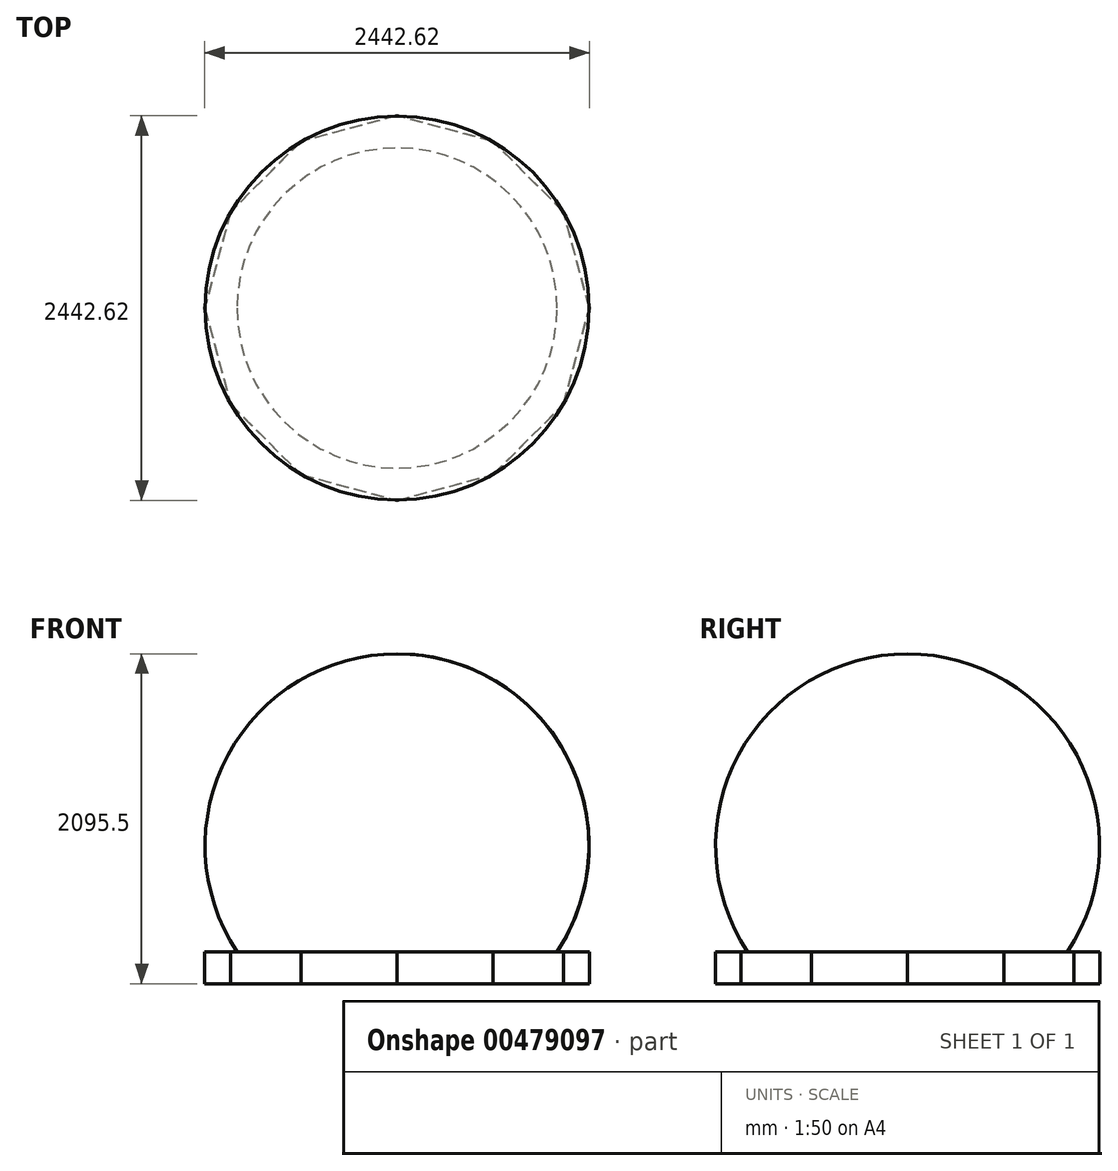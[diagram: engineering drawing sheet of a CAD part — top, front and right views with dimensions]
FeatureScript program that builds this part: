
annotation { "Feature Type Name" : "Feature", "Feature Type Description" : "" }
export const myFeature = defineFeature(function(context is Context, id is Id, definition is map)
    precondition{}
    {
        {
            var Q0;
            Q0=qCreatedBy(makeId("Front.planeOp"),FACE);
            var sketch = newSketch(context, id + "F0", { "sketchPlane" : qUnion([Q0])});
            skArc(sketch, "E0", {"start": v(0, -546.1) * mm, "mid": v(1219.2, 673.1) * mm, "end": v(0, 1892.3) * mm});
            skPoint(sketch, "E1", {"position": v(0, 1892.3) * mm});
            skPoint(sketch, "E2", {"position": v(0, -546.1) * mm});
            skLineSegment(sketch, "E3", {"start": v(0, 1892.3) * mm, "end": v(0, -546.1) * mm});
            skSolve(sketch);
        }
        {
            var Q0;
            Q0 = qSketchRegion(id + "F0", true);
            var Q1;
            Q1=sQuery(id+"F0.wireOp",EDGE,"E3");
            revolve(context, id + "F1", {"entities" : qUnion([Q0]), "axis" : qUnion([Q1]), "revolveType" : RevolveType.FULL});
        }
        {
            var Q0;
            Q0=qCreatedBy(makeId("Top.planeOp"),FACE);
            var sketch = newSketch(context, id + "F2", { "sketchPlane" : qUnion([Q0])});
            skCircle(sketch, "E4", {"center": v(0, 0) * mm, "radius": 1524 * mm});
            skSolve(sketch);
        }
        {
            var Q0;
            Q0=makeQuery(id+"F2.imprint","IMPRINT",FACE,{"disambiguationData":[TD([[makeQuery(id+"F2.imprint","IMPRINT",EDGE,{"derivedFrom":sQuery(id+"F2.wireOp",EDGE,"E4")}),1.0]])]});
            extrude(context, id + "F3", {"entities" : qUnion([Q0]), "operationType" : NewBodyOperationType.REMOVE, "oppositeDirection" : true, "depth" : 914.4 * mm});
        }
        {
            var Q0;
            Q0=makeQuery(id+"F3.boolean.opBoolean","COPY",FACE,{"derivedFrom":makeQuery(id+"F3.opExtrude","CAP_FACE",FACE,{"disambiguationData":[OSD([sQuery(id+"F2.wireOp",EDGE,"E4")])],"isStart":true})});
            var sketch = newSketch(context, id + "F4", { "sketchPlane" : qUnion([Q0])});
            skCircle(sketch, "E5.cCircle", {"center": v(0, 0) * mm, "radius": 1179.7 * mm, "construction": true});
            skLineSegment(sketch, "E5.0", {"start": v(1057.69, 610.66) * mm, "end": v(1221.31, 0) * mm});
            skLineSegment(sketch, "E5.1", {"start": v(1221.31, 0) * mm, "end": v(1057.69, -610.66) * mm});
            skLineSegment(sketch, "E5.2", {"start": v(1057.69, -610.66) * mm, "end": v(610.66, -1057.69) * mm});
            skLineSegment(sketch, "E5.3", {"start": v(610.66, -1057.69) * mm, "end": v(0, -1221.31) * mm});
            skLineSegment(sketch, "E5.4", {"start": v(0, -1221.31) * mm, "end": v(-610.66, -1057.69) * mm});
            skLineSegment(sketch, "E5.5", {"start": v(-610.66, -1057.69) * mm, "end": v(-1057.69, -610.66) * mm});
            skLineSegment(sketch, "E5.6", {"start": v(-1057.69, -610.66) * mm, "end": v(-1221.31, 0) * mm});
            skLineSegment(sketch, "E5.7", {"start": v(-1221.31, 0) * mm, "end": v(-1057.69, 610.66) * mm});
            skLineSegment(sketch, "E5.8", {"start": v(-1057.69, 610.66) * mm, "end": v(-610.66, 1057.69) * mm});
            skLineSegment(sketch, "E5.9", {"start": v(-610.66, 1057.69) * mm, "end": v(0, 1221.31) * mm});
            skLineSegment(sketch, "E5.10", {"start": v(0, 1221.31) * mm, "end": v(610.66, 1057.69) * mm});
            skLineSegment(sketch, "E5.11", {"start": v(610.66, 1057.69) * mm, "end": v(1057.69, 610.66) * mm});
            skPoint(sketch, "E5.0.midPoint", {"position": v(1139.5, 305.33) * mm});
            skLineSegment(sketch, "E6", {"start": v(0, 0) * mm, "end": v(0, 1524) * mm, "construction": true});
            skSolve(sketch);
        }
        {
            var Q0;
            Q0 = qSketchRegion(id + "F4", true);
            extrude(context, id + "F5", {"entities" : qUnion([Q0]), "operationType" : NewBodyOperationType.ADD, "depth" : 203.2 * mm});
        }
    });
